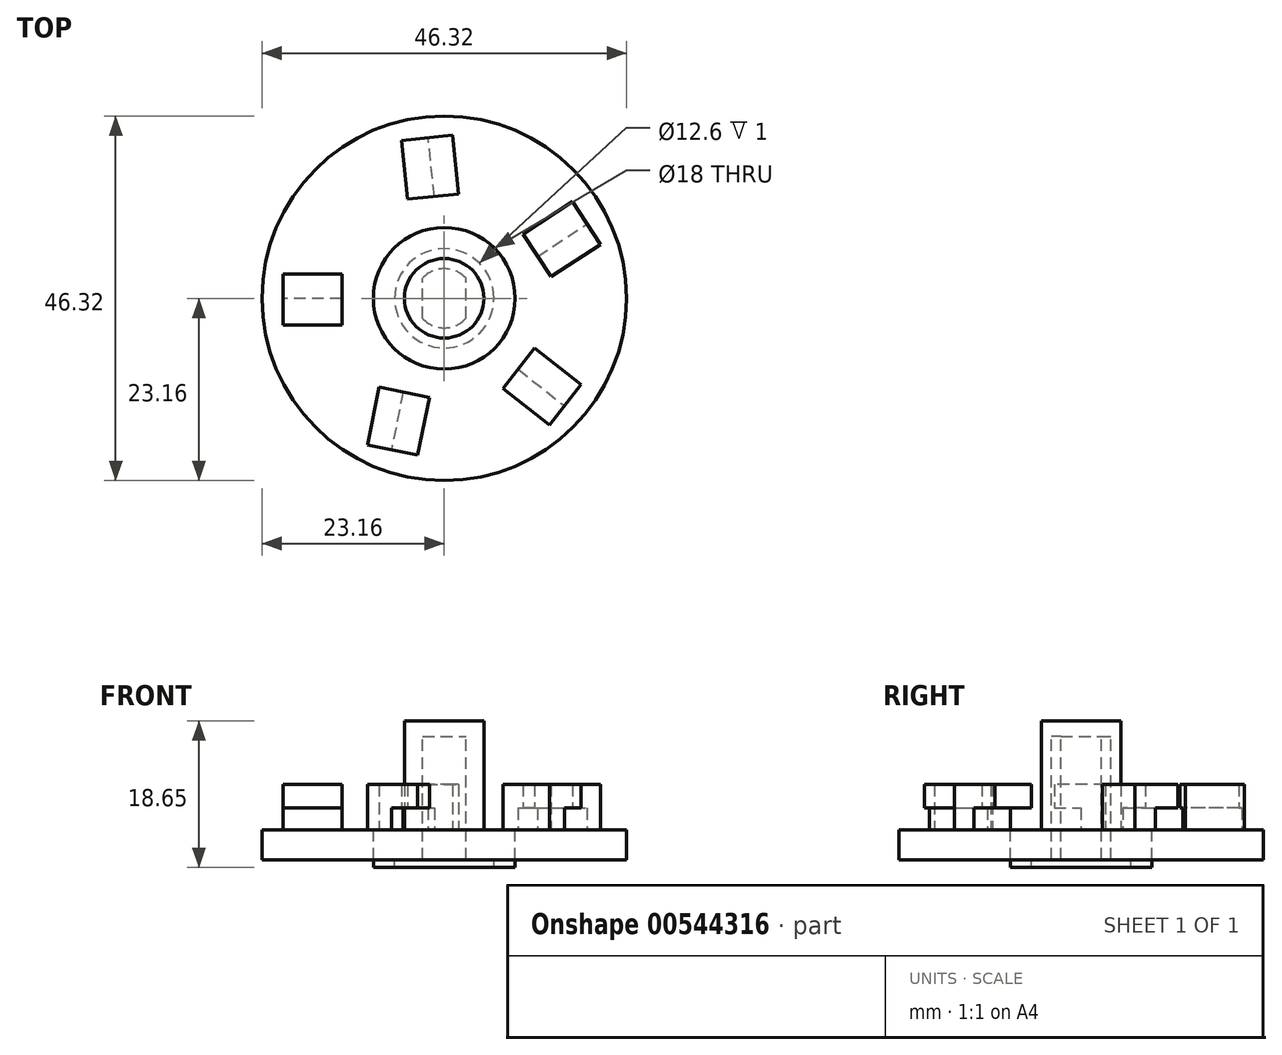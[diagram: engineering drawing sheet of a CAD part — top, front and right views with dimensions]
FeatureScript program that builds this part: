
annotation { "Feature Type Name" : "Feature", "Feature Type Description" : "" }
export const myFeature = defineFeature(function(context is Context, id is Id, definition is map)
    precondition{}
    {
        {
            var Q0;
            Q0=qCreatedBy(makeId("Top.planeOp"),FACE);
            var sketch = newSketch(context, id + "F0", { "sketchPlane" : qUnion([Q0])});
            skCircle(sketch, "E0", {"center": v(0, 0) * mm, "radius": 23.16 * mm});
            skCircle(sketch, "E1", {"center": v(0, 0) * mm, "radius": 6.3 * mm});
            skCircle(sketch, "E2", {"center": v(0, 0) * mm, "radius": 9 * mm});
            skCircle(sketch, "E3", {"center": v(0, 0) * mm, "radius": 5.05 * mm});
            skLineSegment(sketch, "E4", {"start": v(-5.23, -11.9) * mm, "end": v(-6.72, -19.25) * mm});
            skLineSegment(sketch, "E5", {"start": v(-6.72, -19.25) * mm, "end": v(-1.53, -20.3) * mm});
            skLineSegment(sketch, "E6", {"start": v(-1.53, -20.3) * mm, "end": v(-0.03, -12.96) * mm});
            skLineSegment(sketch, "E7", {"start": v(-0.03, -12.96) * mm, "end": v(-5.23, -11.9) * mm});
            skLineSegment(sketch, "E8", {"start": v(-13, 0) * mm, "end": v(-20.5, 0) * mm});
            skLineSegment(sketch, "E9", {"start": v(-20.5, 0) * mm, "end": v(-20.5, -5.3) * mm});
            skLineSegment(sketch, "E10", {"start": v(-20.5, -5.3) * mm, "end": v(-13, -5.3) * mm});
            skLineSegment(sketch, "E11", {"start": v(-13, -5.3) * mm, "end": v(-13, 0) * mm});
            skLineSegment(sketch, "E12", {"start": v(9.37, -9) * mm, "end": v(15.27, -13.65) * mm});
            skLineSegment(sketch, "E13", {"start": v(15.27, -13.65) * mm, "end": v(18.54, -9.48) * mm});
            skLineSegment(sketch, "E14", {"start": v(18.54, -9.48) * mm, "end": v(12.65, -4.84) * mm});
            skLineSegment(sketch, "E15", {"start": v(12.65, -4.84) * mm, "end": v(9.37, -9) * mm});
            skLineSegment(sketch, "E16", {"start": v(11.86, 5.33) * mm, "end": v(18.13, 9.44) * mm});
            skLineSegment(sketch, "E17", {"start": v(18.13, 9.44) * mm, "end": v(15.22, 13.87) * mm});
            skLineSegment(sketch, "E18", {"start": v(15.22, 13.87) * mm, "end": v(8.95, 9.76) * mm});
            skLineSegment(sketch, "E19", {"start": v(8.95, 9.76) * mm, "end": v(11.86, 5.33) * mm});
            skLineSegment(sketch, "E20", {"start": v(-1.25, 12.94) * mm, "end": v(-2.04, 20.4) * mm});
            skLineSegment(sketch, "E21", {"start": v(-2.04, 20.4) * mm, "end": v(-7.31, 19.84) * mm});
            skLineSegment(sketch, "E22", {"start": v(-7.31, 19.84) * mm, "end": v(-6.52, 12.38) * mm});
            skLineSegment(sketch, "E23", {"start": v(-6.52, 12.38) * mm, "end": v(-1.25, 12.94) * mm});
            skLineSegment(sketch, "E24", {"start": v(-1.25, 12.94) * mm, "end": v(1.83, 13.27) * mm});
            skLineSegment(sketch, "E25", {"start": v(1.83, 13.27) * mm, "end": v(1.04, 20.73) * mm});
            skLineSegment(sketch, "E26", {"start": v(1.04, 20.73) * mm, "end": v(-2.04, 20.4) * mm});
            skLineSegment(sketch, "E27", {"start": v(-2.04, 20.4) * mm, "end": v(-5.62, 20.02) * mm});
            skPoint(sketch, "E27.endSnap0", {"position": v(-5.62, 20.02) * mm});
            skLineSegment(sketch, "E28", {"start": v(-5.62, 20.02) * mm, "end": v(-4.83, 12.56) * mm});
            skLineSegment(sketch, "E29", {"start": v(-4.83, 12.56) * mm, "end": v(-1.25, 12.94) * mm});
            skLineSegment(sketch, "E30", {"start": v(18.13, 9.44) * mm, "end": v(19.83, 6.85) * mm});
            skLineSegment(sketch, "E31", {"start": v(19.83, 6.85) * mm, "end": v(13.56, 2.73) * mm});
            skLineSegment(sketch, "E32", {"start": v(13.56, 2.73) * mm, "end": v(11.86, 5.33) * mm});
            skLineSegment(sketch, "E33", {"start": v(9.37, -9) * mm, "end": v(7.46, -11.45) * mm});
            skLineSegment(sketch, "E34", {"start": v(7.46, -11.45) * mm, "end": v(13.35, -16.08) * mm});
            skLineSegment(sketch, "E35", {"start": v(13.35, -16.08) * mm, "end": v(15.27, -13.65) * mm});
            skLineSegment(sketch, "E36", {"start": v(-5.23, -11.9) * mm, "end": v(-8.26, -11.29) * mm});
            skLineSegment(sketch, "E37", {"start": v(-8.26, -11.29) * mm, "end": v(-9.76, -18.63) * mm});
            skLineSegment(sketch, "E38", {"start": v(-9.76, -18.63) * mm, "end": v(-6.72, -19.25) * mm});
            skLineSegment(sketch, "E39", {"start": v(-13, 0) * mm, "end": v(-13, 3.1) * mm});
            skLineSegment(sketch, "E40", {"start": v(-13, 3.1) * mm, "end": v(-20.5, 3.1) * mm});
            skLineSegment(sketch, "E41", {"start": v(-20.5, 3.1) * mm, "end": v(-20.5, 0) * mm});
            skLineSegment(sketch, "E42.left", {"start": v(2.74, -2.58) * mm, "end": v(2.74, 2.58) * mm});
            skLineSegment(sketch, "E42.right", {"start": v(-2.74, -2.58) * mm, "end": v(-2.74, 2.57) * mm});
            skArc(sketch, "E43", {"start": v(0, -3.76) * mm, "mid": v(1.5, -3.45) * mm, "end": v(2.74, -2.58) * mm});
            skArc(sketch, "E44", {"start": v(0, -3.76) * mm, "mid": v(-1.5, -3.45) * mm, "end": v(-2.74, -2.58) * mm});
            skArc(sketch, "E45", {"start": v(0, 3.76) * mm, "mid": v(1.5, 3.45) * mm, "end": v(2.74, 2.58) * mm});
            skArc(sketch, "E46", {"start": v(0, 3.76) * mm, "mid": v(-1.5, 3.45) * mm, "end": v(-2.74, 2.57) * mm});
            skPoint(sketch, "E47.orphan", {"position": v(2.74, -3.76) * mm});
            skPoint(sketch, "E48.orphan", {"position": v(2.74, 3.76) * mm});
            skPoint(sketch, "E49.orphan", {"position": v(-2.74, 3.76) * mm});
            skPoint(sketch, "E42.bottom.end.orphan", {"position": v(-2.74, -3.76) * mm});
            skSolve(sketch);
        }
        {
            var Q0;
            Q0=qSketchRegion(id+"F0",true);
            extrude(context, id + "F1", {"entities" : qUnion([Q0]), "oppositeDirection" : true, "depth" : 3.75 * mm, "offsetDistance" : 25 * mm});
        }
        {
            var Q0;
            Q0=makeQuery(id+"F0.imprint","IMPRINT",FACE,{"disambiguationData":[TD([[makeQuery(id+"F0.imprint","IMPRINT",EDGE,{"derivedFrom":sQuery(id+"F0.wireOp",EDGE,"E1")}),-1.0]])]});
            extrude(context, id + "F2", {"entities" : qUnion([Q0]), "oppositeDirection" : true, "depth" : 4.75 * mm, "offsetDistance" : 25 * mm});
        }
        {
            var Q0;
            Q0=makeQuery(id+"F0.imprint","IMPRINT",FACE,{"disambiguationData":[TD([[makeQuery(id+"F0.imprint","IMPRINT",EDGE,{"derivedFrom":sQuery(id+"F0.wireOp",EDGE,"E20")}),-1.0]])]});
            extrude(context, id + "F3", {"entities" : qUnion([Q0]), "depth" : 5.8 * mm, "offsetDistance" : 25 * mm});
        }
        {
            var Q0;
            Q0=makeQuery(id+"F0.imprint","IMPRINT",FACE,{"disambiguationData":[TD([[makeQuery(id+"F0.imprint","IMPRINT",EDGE,{"derivedFrom":sQuery(id+"F0.wireOp",EDGE,"E20")}),-1.0]])]});
            extrude(context, id + "F4", {"entities" : qUnion([Q0]), "operationType" : NewBodyOperationType.ADD, "oppositeDirection" : true, "depth" : 3.75 * mm, "offsetDistance" : 25 * mm});
        }
        {
            var Q0;
            Q0=makeQuery(id+"F3.opExtrude","SWEPT_FACE",FACE,{"disambiguationData":[OSD([sQuery(id+"F0.wireOp",EDGE,"E20")])]});
            var sketch = newSketch(context, id + "F5", { "sketchPlane" : qUnion([Q0])});
            skLineSegment(sketch, "E50.bottom", {"start": v(-20.5, 5.8) * mm, "end": v(-13, 5.8) * mm});
            skLineSegment(sketch, "E50.top", {"start": v(-20.5, 2.8) * mm, "end": v(-13, 2.8) * mm});
            skLineSegment(sketch, "E50.left", {"start": v(-20.5, 5.8) * mm, "end": v(-20.5, 2.8) * mm});
            skLineSegment(sketch, "E50.right", {"start": v(-13, 5.8) * mm, "end": v(-13, 2.8) * mm});
            skSolve(sketch);
        }
        {
            var Q0;
            Q0=makeQuery(id+"F5.imprint","IMPRINT",FACE,{"disambiguationData":[TD([[makeQuery(id+"F5.imprint","IMPRINT",EDGE,{"derivedFrom":sQuery(id+"F5.wireOp",EDGE,"E50.bottom")}),1.0]])]});
            extrude(context, id + "F6", {"entities" : qUnion([Q0]), "operationType" : NewBodyOperationType.ADD, "depth" : 3.4 * mm, "offsetDistance" : 25 * mm});
        }
        {
            var Q0;
            Q0=makeQuery(id+"F0.imprint","IMPRINT",FACE,{"disambiguationData":[TD([[makeQuery(id+"F0.imprint","IMPRINT",EDGE,{"derivedFrom":sQuery(id+"F0.wireOp",EDGE,"E8")}),-1.0]])]});
            var Q1;
            Q1=makeQuery(id+"F0.imprint","IMPRINT",FACE,{"disambiguationData":[TD([[makeQuery(id+"F0.imprint","IMPRINT",EDGE,{"derivedFrom":sQuery(id+"F0.wireOp",EDGE,"E16")}),-1.0]])]});
            var Q2;
            Q2=makeQuery(id+"F0.imprint","IMPRINT",FACE,{"disambiguationData":[TD([[makeQuery(id+"F0.imprint","IMPRINT",EDGE,{"derivedFrom":sQuery(id+"F0.wireOp",EDGE,"E12")}),-1.0]])]});
            var Q3;
            Q3=makeQuery(id+"F0.imprint","IMPRINT",FACE,{"disambiguationData":[TD([[makeQuery(id+"F0.imprint","IMPRINT",EDGE,{"derivedFrom":sQuery(id+"F0.wireOp",EDGE,"E4")}),-1.0]])]});
            extrude(context, id + "F7", {"entities" : qUnion([Q0, Q1, Q2, Q3]), "operationType" : NewBodyOperationType.ADD, "depth" : 5.8 * mm, "offsetDistance" : 25 * mm});
        }
        {
            var Q0;
            Q0=makeQuery(id+"F7.opExtrude","SWEPT_FACE",FACE,{"disambiguationData":[OSD([sQuery(id+"F0.wireOp",EDGE,"E8")])]});
            var sketch = newSketch(context, id + "F8", { "sketchPlane" : qUnion([Q0])});
            skLineSegment(sketch, "E51", {"start": v(-20.5, 5.8) * mm, "end": v(-20.5, 2.8) * mm});
            skLineSegment(sketch, "E52", {"start": v(-20.5, 2.8) * mm, "end": v(-13, 2.8) * mm});
            skLineSegment(sketch, "E53", {"start": v(-13, 2.8) * mm, "end": v(-13, 5.8) * mm});
            skSolve(sketch);
        }
        {
            var Q0;
            Q0=makeQuery(id+"F8.imprint","IMPRINT",FACE,{"disambiguationData":[TD([[makeQuery(id+"F8.imprint","IMPRINT",EDGE,{"derivedFrom":sQuery(id+"F8.wireOp",EDGE,"E51")}),1.0]])]});
            extrude(context, id + "F9", {"entities" : qUnion([Q0]), "operationType" : NewBodyOperationType.ADD, "depth" : 3.4 * mm, "offsetDistance" : 25 * mm});
        }
        {
            var Q0;
            Q0=makeQuery(id+"F7.opExtrude","SWEPT_FACE",FACE,{"disambiguationData":[OSD([sQuery(id+"F0.wireOp",EDGE,"E4")])]});
            var sketch = newSketch(context, id + "F10", { "sketchPlane" : qUnion([Q0])});
            skLineSegment(sketch, "E54", {"start": v(-20.2, 5.8) * mm, "end": v(-20.2, 2.8) * mm});
            skLineSegment(sketch, "E55", {"start": v(-20.2, 2.8) * mm, "end": v(-12.7, 2.8) * mm});
            skLineSegment(sketch, "E56", {"start": v(-12.7, 2.8) * mm, "end": v(-12.7, 5.8) * mm});
            skSolve(sketch);
        }
        {
            var Q0;
            Q0=makeQuery(id+"F10.imprint","IMPRINT",FACE,{"disambiguationData":[TD([[makeQuery(id+"F10.imprint","IMPRINT",EDGE,{"derivedFrom":sQuery(id+"F10.wireOp",EDGE,"E54")}),1.0]])]});
            extrude(context, id + "F11", {"entities" : qUnion([Q0]), "operationType" : NewBodyOperationType.ADD, "depth" : 3.4 * mm, "offsetDistance" : 25 * mm});
        }
        {
            var Q0;
            Q0=makeQuery(id+"F0.imprint","IMPRINT",FACE,{"disambiguationData":[TD([[makeQuery(id+"F0.imprint","IMPRINT",EDGE,{"derivedFrom":sQuery(id+"F0.wireOp",EDGE,"E8")}),-1.0]])]});
            var Q1;
            Q1=makeQuery(id+"F0.imprint","IMPRINT",FACE,{"disambiguationData":[TD([[makeQuery(id+"F0.imprint","IMPRINT",EDGE,{"derivedFrom":sQuery(id+"F0.wireOp",EDGE,"E4")}),-1.0]])]});
            var Q2;
            Q2=makeQuery(id+"F0.imprint","IMPRINT",FACE,{"disambiguationData":[TD([[makeQuery(id+"F0.imprint","IMPRINT",EDGE,{"derivedFrom":sQuery(id+"F0.wireOp",EDGE,"E16")}),-1.0]])]});
            var Q3;
            Q3=makeQuery(id+"F0.imprint","IMPRINT",FACE,{"disambiguationData":[TD([[makeQuery(id+"F0.imprint","IMPRINT",EDGE,{"derivedFrom":sQuery(id+"F0.wireOp",EDGE,"E12")}),-1.0]])]});
            extrude(context, id + "F12", {"entities" : qUnion([Q0, Q1, Q2, Q3]), "oppositeDirection" : true, "depth" : 3.75 * mm, "offsetDistance" : 25 * mm});
        }
        {
            var Q0;
            Q0=makeQuery(id+"F7.opExtrude","SWEPT_FACE",FACE,{"disambiguationData":[OSD([sQuery(id+"F0.wireOp",EDGE,"E12")])]});
            var sketch = newSketch(context, id + "F13", { "sketchPlane" : qUnion([Q0])});
            skLineSegment(sketch, "E57", {"start": v(-12.94, 5.8) * mm, "end": v(-12.94, 2.8) * mm});
            skLineSegment(sketch, "E58", {"start": v(-12.94, 2.8) * mm, "end": v(-20.44, 2.8) * mm});
            skLineSegment(sketch, "E59", {"start": v(-20.44, 2.8) * mm, "end": v(-20.44, 5.8) * mm});
            skSolve(sketch);
        }
        {
            var Q0;
            Q0=makeQuery(id+"F13.imprint","IMPRINT",FACE,{"disambiguationData":[TD([[makeQuery(id+"F13.imprint","IMPRINT",EDGE,{"derivedFrom":sQuery(id+"F13.wireOp",EDGE,"E57")}),-1.0]])]});
            extrude(context, id + "F14", {"entities" : qUnion([Q0]), "operationType" : NewBodyOperationType.ADD, "depth" : 3.4 * mm, "offsetDistance" : 25 * mm});
        }
        {
            var Q0;
            Q0=makeQuery(id+"F7.opExtrude","SWEPT_FACE",FACE,{"disambiguationData":[OSD([sQuery(id+"F0.wireOp",EDGE,"E16")])]});
            var sketch = newSketch(context, id + "F15", { "sketchPlane" : qUnion([Q0])});
            skLineSegment(sketch, "E60", {"start": v(-12.84, 5.8) * mm, "end": v(-12.84, 2.8) * mm});
            skLineSegment(sketch, "E61", {"start": v(-12.84, 2.8) * mm, "end": v(-20.34, 2.8) * mm});
            skLineSegment(sketch, "E62", {"start": v(-20.34, 2.8) * mm, "end": v(-20.34, 5.8) * mm});
            skSolve(sketch);
        }
        {
            var Q0;
            Q0=makeQuery(id+"F15.imprint","IMPRINT",FACE,{"disambiguationData":[TD([[makeQuery(id+"F15.imprint","IMPRINT",EDGE,{"derivedFrom":sQuery(id+"F15.wireOp",EDGE,"E60")}),-1.0]])]});
            extrude(context, id + "F16", {"entities" : qUnion([Q0]), "operationType" : NewBodyOperationType.ADD, "depth" : 3.4 * mm, "offsetDistance" : 25 * mm});
        }
        {
            var Q0;
            Q0=makeQuery(id+"F0.imprint","IMPRINT",FACE,{"disambiguationData":[TD([[makeQuery(id+"F0.imprint","IMPRINT",EDGE,{"derivedFrom":sQuery(id+"F0.wireOp",EDGE,"E1")}),1.0]])]});
            extrude(context, id + "F17", {"entities" : qUnion([Q0]), "operationType" : NewBodyOperationType.ADD, "oppositeDirection" : true, "depth" : 3.75 * mm, "offsetDistance" : 25 * mm});
        }
        {
            var Q0;
            Q0=makeQuery(id+"F0.imprint","IMPRINT",FACE,{"disambiguationData":[TD([[makeQuery(id+"F0.imprint","IMPRINT",EDGE,{"derivedFrom":sQuery(id+"F0.wireOp",EDGE,"E3")}),1.0]])]});
            extrude(context, id + "F18", {"entities" : qUnion([Q0]), "operationType" : NewBodyOperationType.ADD, "oppositeDirection" : true, "depth" : 3.75 * mm, "offsetDistance" : 25 * mm});
        }
        {
            var Q0;
            Q0=makeQuery(id+"F0.imprint","IMPRINT",FACE,{"disambiguationData":[TD([[makeQuery(id+"F0.imprint","IMPRINT",EDGE,{"derivedFrom":sQuery(id+"F0.wireOp",EDGE,"E3")}),1.0]])]});
            extrude(context, id + "F19", {"entities" : qUnion([Q0]), "operationType" : NewBodyOperationType.ADD, "depth" : 11.9 * mm, "offsetDistance" : 25 * mm});
        }
        {
            var Q0;
            Q0=makeQuery(id+"F19.opExtrude","CAP_FACE",FACE,{"disambiguationData":[OSD([sQuery(id+"F0.wireOp",EDGE,"E3"),sQuery(id+"F0.wireOp",EDGE,"E42.left"),sQuery(id+"F0.wireOp",EDGE,"E42.right"),sQuery(id+"F0.wireOp",EDGE,"E43"),sQuery(id+"F0.wireOp",EDGE,"E44"),sQuery(id+"F0.wireOp",EDGE,"E45"),sQuery(id+"F0.wireOp",EDGE,"E46")])],"isStart":false});
            var sketch = newSketch(context, id + "F20", { "sketchPlane" : qUnion([Q0])});
            skCircle(sketch, "E63", {"center": v(0, 0) * mm, "radius": 5.05 * mm});
            skSolve(sketch);
        }
        {
            var Q0;
            Q0=makeQuery(id+"F20.imprint","IMPRINT",FACE,{"disambiguationData":[TD([[makeQuery(id+"F20.imprint","IMPRINT",EDGE,{"derivedFrom":sQuery(id+"F20.wireOp",EDGE,"E63")}),1.0]])]});
            var Q1;
            Q1=makeQuery(id+"F20.imprint","IMPRINT",FACE,{"disambiguationData":[TD([[makeQuery(id+"F20.imprint","IMPRINT",EDGE,{"derivedFrom":makeQuery(id+"F19.opExtrude","CAP_EDGE",EDGE,{"disambiguationData":[OSD([sQuery(id+"F0.wireOp",EDGE,"E42.left")])],"isStart":false})}),1.0]])]});
            extrude(context, id + "F21", {"entities" : qUnion([Q0, Q1]), "operationType" : NewBodyOperationType.ADD, "depth" : 2 * mm, "offsetDistance" : 25 * mm});
        }
        {
            var Q0;
            Q0=makeQuery(id+"F0.imprint","IMPRINT",FACE,{"disambiguationData":[TD([[makeQuery(id+"F0.imprint","IMPRINT",EDGE,{"derivedFrom":sQuery(id+"F0.wireOp",EDGE,"E21")}),1.0]])]});
            var Q1;
            Q1=makeQuery(id+"F0.imprint","IMPRINT",FACE,{"disambiguationData":[TD([[makeQuery(id+"F0.imprint","IMPRINT",EDGE,{"derivedFrom":sQuery(id+"F0.wireOp",EDGE,"E20")}),1.0]])]});
            var Q2;
            Q2=makeQuery(id+"F0.imprint","IMPRINT",FACE,{"disambiguationData":[TD([[makeQuery(id+"F0.imprint","IMPRINT",EDGE,{"derivedFrom":sQuery(id+"F0.wireOp",EDGE,"E8")}),1.0]])]});
            var Q3;
            Q3=makeQuery(id+"F0.imprint","IMPRINT",FACE,{"disambiguationData":[TD([[makeQuery(id+"F0.imprint","IMPRINT",EDGE,{"derivedFrom":sQuery(id+"F0.wireOp",EDGE,"E4")}),1.0]])]});
            var Q4;
            Q4=makeQuery(id+"F0.imprint","IMPRINT",FACE,{"disambiguationData":[TD([[makeQuery(id+"F0.imprint","IMPRINT",EDGE,{"derivedFrom":sQuery(id+"F0.wireOp",EDGE,"E12")}),1.0]])]});
            var Q5;
            Q5=makeQuery(id+"F0.imprint","IMPRINT",FACE,{"disambiguationData":[TD([[makeQuery(id+"F0.imprint","IMPRINT",EDGE,{"derivedFrom":sQuery(id+"F0.wireOp",EDGE,"E16")}),1.0]])]});
            extrude(context, id + "F22", {"entities" : qUnion([Q0, Q1, Q2, Q3, Q4, Q5]), "operationType" : NewBodyOperationType.ADD, "oppositeDirection" : true, "depth" : 3.75 * mm, "offsetDistance" : 25 * mm});
        }
    });
